# Revit family: Hitachi_RCIMW-20-2_50-2_LOD400
name_source: partatom
category: Equipement de génie climatique
revit_build: Autodesk Revit 2018 (Build: 20190510_1515(x64)
units: mm (PartAtom-declared; Revit-internal decimal feet)

## family parameters
Basée sur le plan de construction = Oui
Cote de connecteur circulaire = Utiliser le diamètre
Couper avec des vides une fois chargée = Oui
Numéro OmniClass = 23.75.00.00
Partagée = Oui
Point de calcul de pièce = Oui
Titre OmniClass = Climate Control (HVAC)
Toujours verticalement = Oui
Type d'élément = Normal

## types (4) — shared parameters
4Pipes = Non
A = 572 mm
D_QC_IN = 15 mm  [stored 0.0492126 ft]
D_Q_C_OUT = 15 mm  [stored 0.0492126 ft]
Description = Fan Coil Unit - RCIMW
Electric Battery = Oui
Elévation par défaut = 1219 mm
Fabricant = Hitachi Air Conditioning Europe SAS
Image du type = 600x600.jpg (2)
Lookup Table Name = dataS
Modèle = RCIMW
S = 348 mm
ScheduleType |RF| = ita>eng skystar dimensionamento
THIN_def = 50 °C
cpa = 1.0050 J/(g·°C)
cph = 4.1860 J/(g·°C)
hole Celing = 582 mm  [stored 1.90945 ft]
rho_a = 1.2000 kg/m³
rho_h = 1000.2970 kg/m³
side machine = 572 mm
zero-valued in all types: BVc, COBie_Cost, COBie_ExpectedLife, COBie_ReplacementCost, COBie_WarrantyDurationLabour, COBie_WarrantyDurationParts

## per-type parameters (varying)
| type | Taglia |
| RCIMW 20-2 | 2 |
| RCIMW 25-2 | 12 |
| RCIMW 40-2 | 22 |
| RCIMW 50-2 | 32 |

note: [stored X ft] marks values corroborated as IEEE doubles in the binary element streams (Revit-internal decimal feet)
